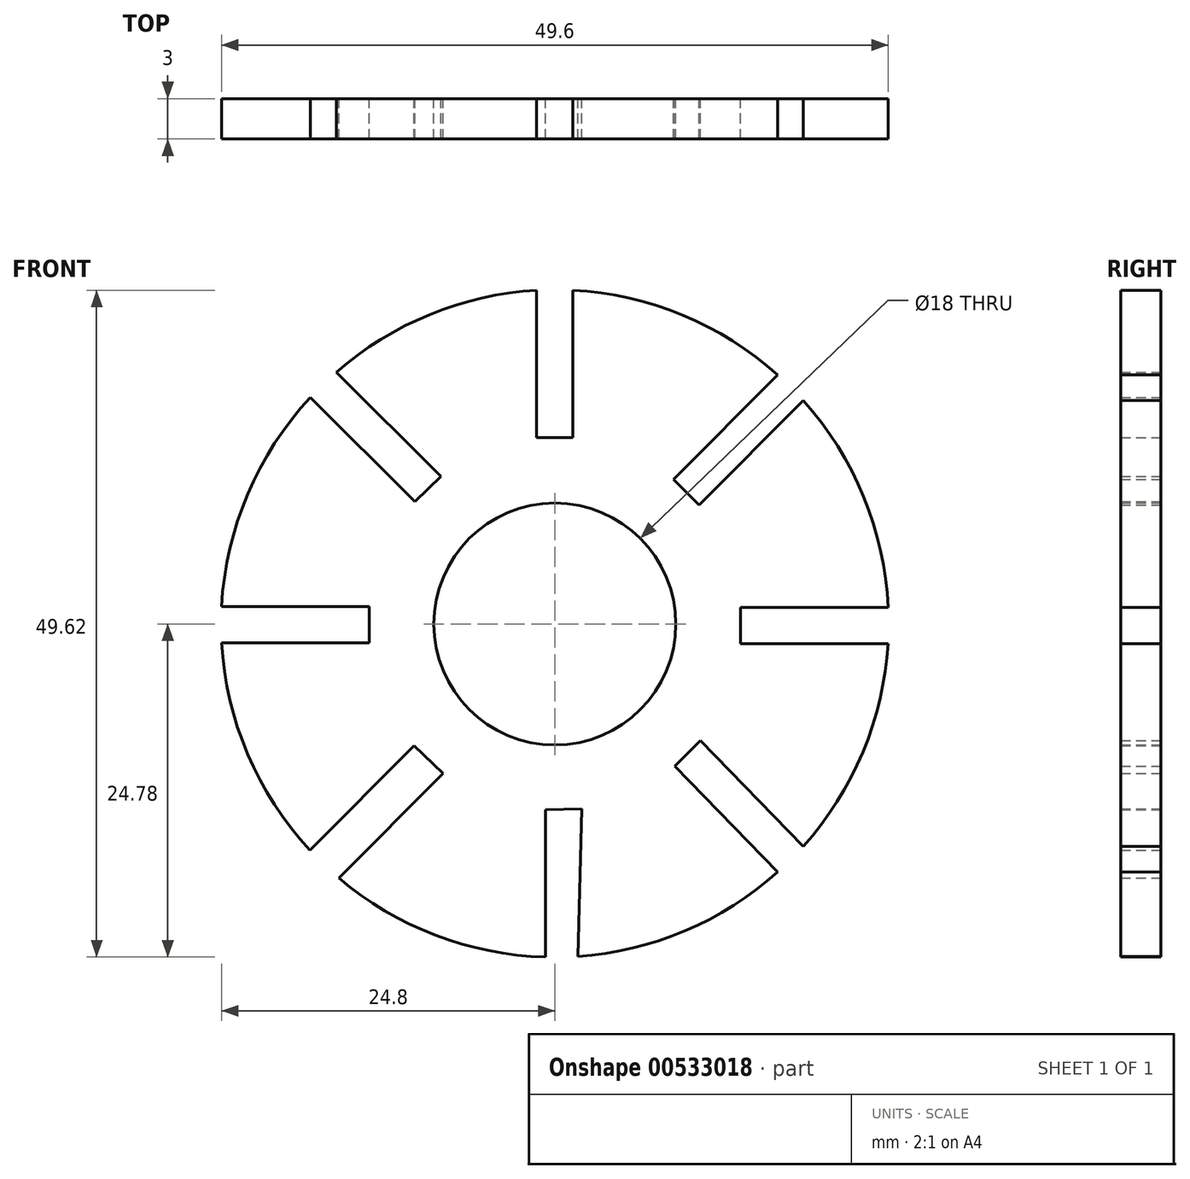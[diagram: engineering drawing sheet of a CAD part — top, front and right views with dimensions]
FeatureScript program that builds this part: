
annotation { "Feature Type Name" : "Feature", "Feature Type Description" : "" }
export const myFeature = defineFeature(function(context is Context, id is Id, definition is map)
    precondition{}
    {
        {
            var Q0;
            Q0=qCreatedBy(makeId("Front.planeOp"),FACE);
            var sketch = newSketch(context, id + "F0", { "sketchPlane" : qUnion([Q0])});
            skLineSegment(sketch, "E0.top", {"start": v(1.35, 13.86) * mm, "end": v(-1.35, 13.86) * mm});
            skLineSegment(sketch, "E0.left", {"start": v(1.35, 24.84) * mm, "end": v(1.35, 13.86) * mm});
            skLineSegment(sketch, "E0.right", {"start": v(-1.35, 24.84) * mm, "end": v(-1.35, 13.86) * mm});
            skPoint(sketch, "E0.middle", {"position": v(0, 22.64) * mm});
            skLineSegment(sketch, "E1.1.0", {"start": v(-16.25, 18.74) * mm, "end": v(-8.49, 10.98) * mm});
            skPoint(sketch, "E1.1.1", {"position": v(-16.05, 15.9) * mm});
            skLineSegment(sketch, "E1.1.2", {"start": v(-8.49, 10.98) * mm, "end": v(-10.42, 9.1) * mm});
            skLineSegment(sketch, "E1.1.3", {"start": v(-18.19, 16.86) * mm, "end": v(-10.42, 9.1) * mm});
            skLineSegment(sketch, "E1.2.0", {"start": v(-24.8, 1.31) * mm, "end": v(-13.82, 1.31) * mm});
            skPoint(sketch, "E1.2.1", {"position": v(-22.64, -0.22) * mm});
            skLineSegment(sketch, "E1.2.2", {"start": v(-13.82, 1.31) * mm, "end": v(-13.81, -1.39) * mm});
            skLineSegment(sketch, "E1.2.3", {"start": v(-24.8, -1.39) * mm, "end": v(-13.81, -1.39) * mm});
            skLineSegment(sketch, "E1.3.0", {"start": v(-18.23, -16.82) * mm, "end": v(-10.47, -9.06) * mm});
            skPoint(sketch, "E1.3.1", {"position": v(-15.9, -16.27) * mm});
            skLineSegment(sketch, "E1.3.2", {"start": v(-10.47, -9.06) * mm, "end": v(-8.31, -11.12) * mm});
            skLineSegment(sketch, "E1.3.3", {"start": v(-16.08, -18.89) * mm, "end": v(-8.31, -11.12) * mm});
            skLineSegment(sketch, "E1.4.0", {"start": v(-0.7, -24.78) * mm, "end": v(-0.7, -13.8) * mm});
            skPoint(sketch, "E1.4.1", {"position": v(0.22, -22.86) * mm});
            skLineSegment(sketch, "E1.4.2", {"start": v(-0.7, -13.8) * mm, "end": v(2, -13.76) * mm});
            skLineSegment(sketch, "E1.4.3", {"start": v(1.7, -24.73) * mm, "end": v(2, -13.76) * mm});
            skLineSegment(sketch, "E1.5.0", {"start": v(16.58, -18.45) * mm, "end": v(8.91, -10.59) * mm});
            skPoint(sketch, "E1.5.1", {"position": v(16.27, -16.12) * mm});
            skLineSegment(sketch, "E1.5.2", {"start": v(8.91, -10.59) * mm, "end": v(10.82, -8.68) * mm});
            skLineSegment(sketch, "E1.5.3", {"start": v(18.49, -16.54) * mm, "end": v(10.82, -8.68) * mm});
            skLineSegment(sketch, "E1.6.0", {"start": v(24.79, -1.45) * mm, "end": v(13.8, -1.45) * mm});
            skPoint(sketch, "E1.6.1", {"position": v(22.86, 0) * mm});
            skLineSegment(sketch, "E1.6.2", {"start": v(13.8, -1.45) * mm, "end": v(13.82, 1.25) * mm});
            skLineSegment(sketch, "E1.6.3", {"start": v(24.8, 1.25) * mm, "end": v(13.82, 1.25) * mm});
            skLineSegment(sketch, "E1.7.0", {"start": v(18.49, 16.62) * mm, "end": v(10.72, 8.86) * mm});
            skPoint(sketch, "E1.7.1", {"position": v(16.12, 16.05) * mm});
            skLineSegment(sketch, "E1.7.2", {"start": v(10.72, 8.86) * mm, "end": v(8.81, 10.76) * mm});
            skLineSegment(sketch, "E1.7.3", {"start": v(16.58, 18.53) * mm, "end": v(8.81, 10.76) * mm});
            skPoint(sketch, "E1.center", {"position": v(0.11, -0.11) * mm});
            skCircle(sketch, "E2", {"center": v(0, 0) * mm, "radius": 9 * mm});
            skArc(sketch, "E3", {"start": v(-1.35, 24.84) * mm, "mid": v(-9.3, 23.02) * mm, "end": v(-16.25, 18.74) * mm});
            skArc(sketch, "E4", {"start": v(-24.8, -1.39) * mm, "mid": v(-22.85, -9.67) * mm, "end": v(-18.23, -16.82) * mm});
            skPoint(sketch, "E5.orphan", {"position": v(1.35, 31.42) * mm});
            skPoint(sketch, "E6.orphan", {"position": v(-1.35, 31.42) * mm});
            skPoint(sketch, "E7.orphan", {"position": v(-20.91, 23.4) * mm});
            skPoint(sketch, "E8.orphan", {"position": v(-22.6, 21.27) * mm});
            skArc(sketch, "E9.trimOffspring", {"start": v(-18.19, 16.86) * mm, "mid": v(-22.85, 9.66) * mm, "end": v(-24.8, 1.31) * mm});
            skArc(sketch, "E10.trimOffspring", {"start": v(16.58, 18.53) * mm, "mid": v(9.5, 22.98) * mm, "end": v(1.35, 24.84) * mm});
            skArc(sketch, "E11.trimOffspring", {"start": v(24.8, 1.25) * mm, "mid": v(22.97, 9.48) * mm, "end": v(18.49, 16.62) * mm});
            skArc(sketch, "E12.trimOffspring", {"start": v(18.49, -16.54) * mm, "mid": v(22.92, -9.53) * mm, "end": v(24.79, -1.45) * mm});
            skPoint(sketch, "E13.orphan", {"position": v(1.51, -31.76) * mm});
            skPoint(sketch, "E14.orphan", {"position": v(-0.71, -31.32) * mm});
            skArc(sketch, "E15.trimOffspring", {"start": v(1.7, -24.73) * mm, "mid": v(9.67, -22.83) * mm, "end": v(16.58, -18.45) * mm});
            skArc(sketch, "E16.trimOffspring", {"start": v(-16.08, -18.89) * mm, "mid": v(-8.9, -23.15) * mm, "end": v(-0.7, -24.78) * mm});
            skSolve(sketch);
        }
        {
            var Q0;
            {var subQ16=sQuery(id+"F0.wireOp",EDGE,"E0.top");Q0=makeQuery(id+"F0.imprint","IMPRINT",FACE,{"disambiguationData":[TD([[makeQuery(id+"F0.imprint","IMPRINT",EDGE,{"derivedFrom":subQ16}),1.0]])]});}
            extrude(context, id + "F1", {"entities" : qUnion([Q0]), "depth" : 3 * mm, "offsetDistance" : 25 * mm});
        }
    });
